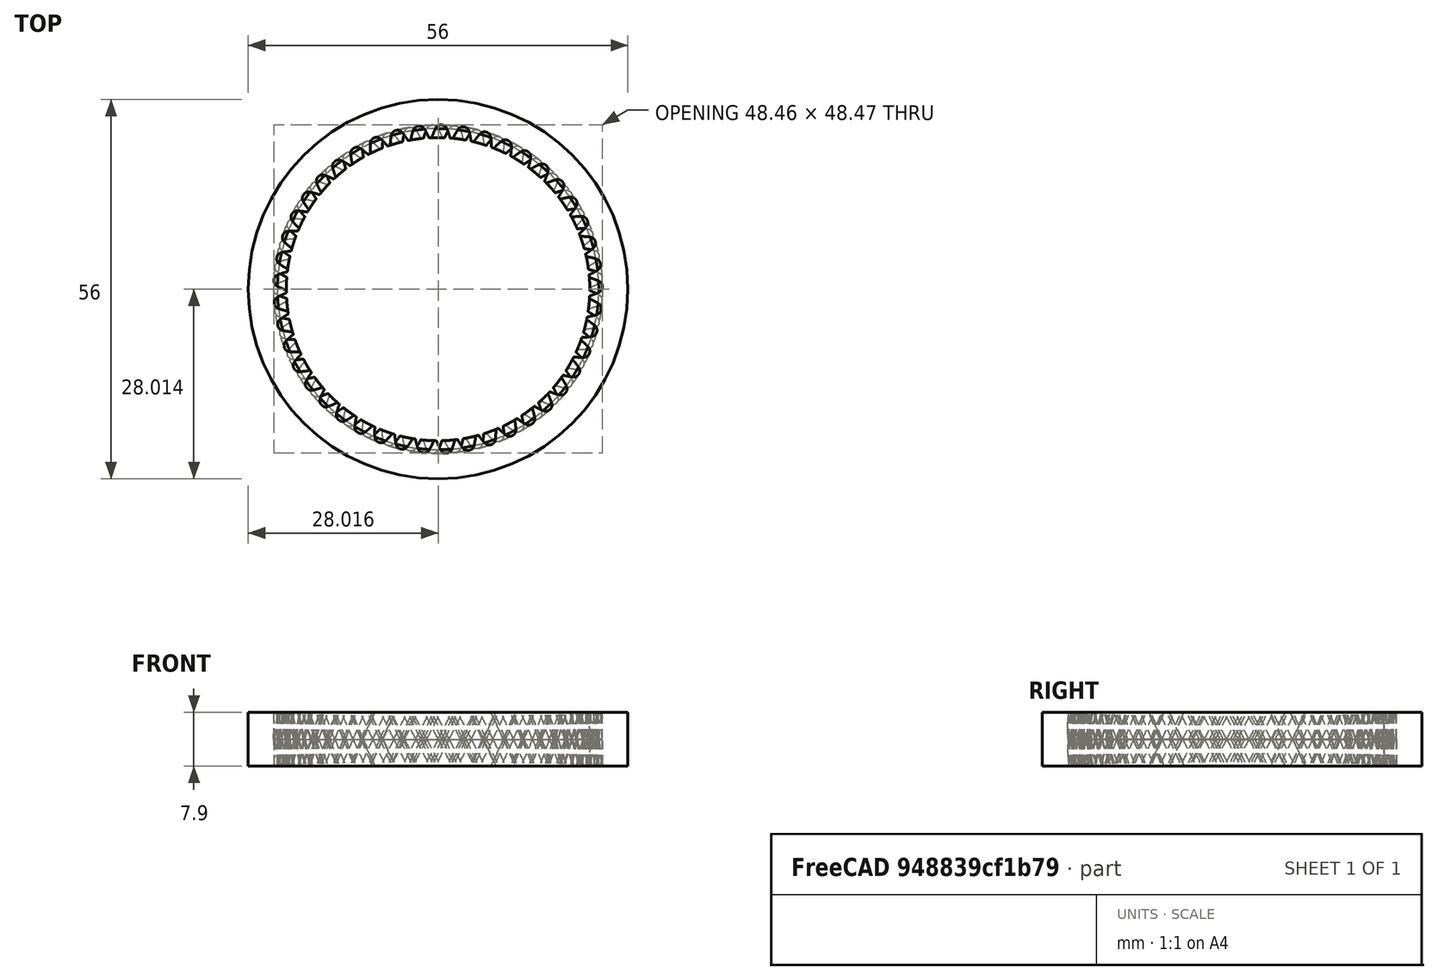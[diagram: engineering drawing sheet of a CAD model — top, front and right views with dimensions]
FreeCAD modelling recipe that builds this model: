
FCSTD DOCUMENT  (FreeCAD 0.17R13541 (Git))
Label: Gear5e
License: All rights reserved
LicenseURL: http://en.wikipedia.org/wiki/All_rights_reserved
objects: Part::Helix×2, Part::Sweep×2, Part::Part2DObjectPython×1, Part::Offset2D×1, Part::Fuse×1, Part::Cylinder×1, Part::Cut×1
note: 9 computed .brp shape members not serialized (recipe doc carries the construction recipe); baked Part::Feature solids carry a one-line shape summary decoded from their .brp

FEATURE [Part::Part2DObjectPython] InvoluteGear  # Draft 2D object (typed FeaturePython)
  ExternalGear = false
  HighPrecision = true
  Modules = 1
  NumberOfTeeth = 45
  PressureAngle = 20
FEATURE [Part::Offset2D] Offset2D
  Fill = false
  Intersection = false
  Join = 1
  Mode = 1
  SelfIntersection = false
  Source = -> InvoluteGear
  Value = 0.5
FEATURE [Part::Helix] Helix
  Angle = 0
  AttacherType = Attacher::AttachEngine3D
  Height = 4
  LocalCoord = 0
  Pitch = 290.32
  Radius = 23
  Style = 1
FEATURE [Part::Helix] Helix001
  Angle = 0
  AttacherType = Attacher::AttachEngine3D
  Height = 4
  LocalCoord = 1
  Pitch = 290.32
  Placement = pos=(0,0,0) rot=(1,0,0;3.14159rad)
  Radius = 23
  Style = 1
FEATURE [Part::Sweep] Sweep001
  Frenet = true
  Sections = -> [Offset2D]
  Solid = true
  Spine = -> Helix [Edge1]
  Transition = 1
FEATURE [Part::Sweep] Sweep
  Frenet = true
  Sections = -> [Offset2D]
  Solid = true
  Spine = -> Helix001 [Edge1]
  Transition = 1
FEATURE [Part::Fuse] Fusion
  Base = -> Sweep001
  Tool = -> Sweep
FEATURE [Part::Cylinder] Cylinder
  Angle = 360
  AttacherType = Attacher::AttachEngine3D
  Height = 7.9
  Placement = pos=(0,0,-3.95) rot=(0,0,1;0rad)
  Radius = 28
FEATURE [Part::Cut] Cut
  Base = -> Cylinder
  Tool = -> Fusion
